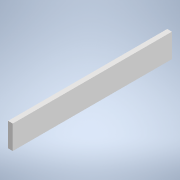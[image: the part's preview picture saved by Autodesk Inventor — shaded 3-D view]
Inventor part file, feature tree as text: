
AUTODESK INVENTOR PART (.ipt)
format: ipt  version: 2021 (Build 250183000, 183)  size: 89,600 bytes
history: native  units: in
note: dims shown in document units (in); Inventor stores cm internally (conversion verified against a paired STEP export)
features: extrude x1, sketch x1
ambient origin geometry x8: Origin, YZ Plane, XZ Plane, XY Plane, X Axis, Y Axis, Z Axis, Center Point
bodies: Solid1 (feature_tree)
feature tree (2):
  extrude  "Extrusion1"  [1 undecoded]
  sketch  "Sketch1"  dims[d0=16.9291in d1=0.0in]
note: 1 required parameter value undecoded (feature->parameter linkage not recoverable at this tier; creation-order binding heuristic only, values carry confidence <= 0.55)
